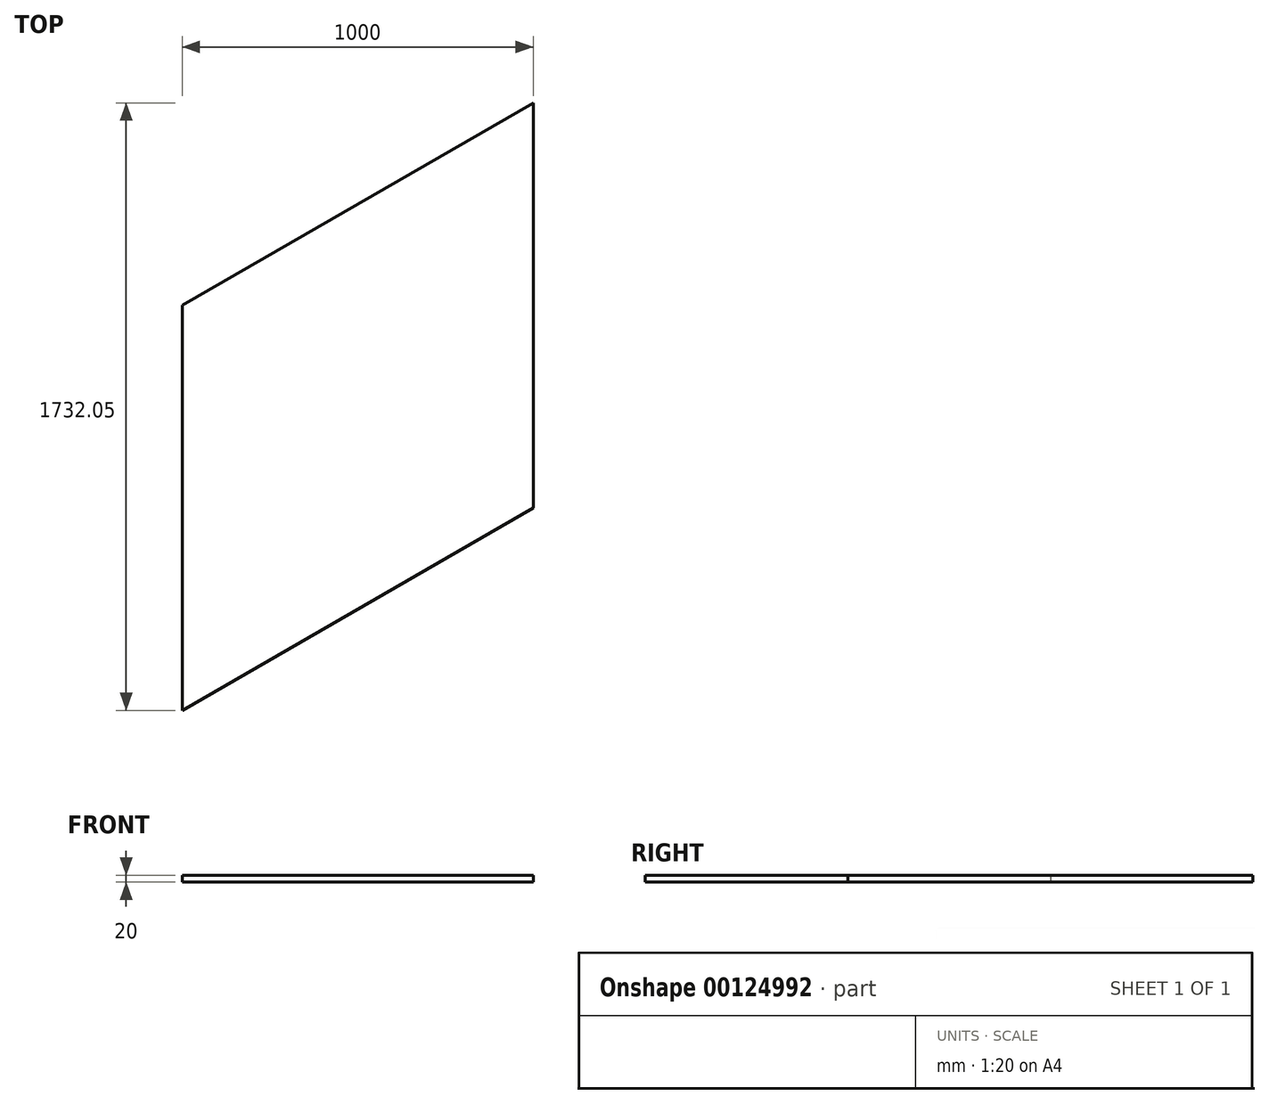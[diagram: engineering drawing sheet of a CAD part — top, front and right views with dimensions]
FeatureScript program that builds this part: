
annotation { "Feature Type Name" : "Feature", "Feature Type Description" : "" }
export const myFeature = defineFeature(function(context is Context, id is Id, definition is map)
    precondition{}
    {
        {
            var Q0;
            Q0=qCreatedBy(makeId("Top.planeOp"),FACE);
            var sketch = newSketch(context, id + "F0", { "sketchPlane" : qUnion([Q0])});
            skCircle(sketch, "E0.cCircle", {"center": v(0, 0) * mm, "radius": 1000 * mm, "construction": true});
            skLineSegment(sketch, "E0.0", {"start": v(1000, 577.35) * mm, "end": v(1000, -577.35) * mm});
            skLineSegment(sketch, "E0.1", {"start": v(1000, -577.35) * mm, "end": v(0, -1154.7) * mm});
            skLineSegment(sketch, "E0.2", {"start": v(0, -1154.7) * mm, "end": v(-1000, -577.35) * mm});
            skLineSegment(sketch, "E0.3", {"start": v(-1000, -577.35) * mm, "end": v(-1000, 577.35) * mm});
            skLineSegment(sketch, "E0.4", {"start": v(-1000, 577.35) * mm, "end": v(0, 1154.7) * mm});
            skLineSegment(sketch, "E0.5", {"start": v(0, 1154.7) * mm, "end": v(1000, 577.35) * mm});
            skPoint(sketch, "E0.0.midPoint", {"position": v(1000, 0) * mm});
            skLineSegment(sketch, "E1", {"start": v(-1000, -577.35) * mm, "end": v(0, 1154.7) * mm, "construction": true});
            skLineSegment(sketch, "E2.MirrorCS", {"start": v(0, 0) * mm, "end": v(0, 1154.7) * mm});
            skLineSegment(sketch, "E3.MirrorCS", {"start": v(-1000, -577.35) * mm, "end": v(0, 0) * mm});
            skLineSegment(sketch, "E4", {"start": v(0, 0) * mm, "end": v(1000, -577.35) * mm});
            skLineSegment(sketch, "E5", {"start": v(-500, 866.03) * mm, "end": v(-500, 288.68) * mm});
            skLineSegment(sketch, "E6", {"start": v(-500, 288.68) * mm, "end": v(0, 577.35) * mm});
            skLineSegment(sketch, "E7", {"start": v(-500, 288.68) * mm, "end": v(-1000, 0) * mm});
            skLineSegment(sketch, "E8", {"start": v(-500, 288.68) * mm, "end": v(-500, -288.68) * mm});
            skLineSegment(sketch, "E9.1.0", {"start": v(0, -577.35) * mm, "end": v(-500, -288.68) * mm});
            skLineSegment(sketch, "E9.1.1", {"start": v(-500, -866.03) * mm, "end": v(0, -577.35) * mm});
            skLineSegment(sketch, "E9.1.2", {"start": v(0, -577.35) * mm, "end": v(500, -866.03) * mm});
            skLineSegment(sketch, "E9.1.3", {"start": v(0, -577.35) * mm, "end": v(500, -288.68) * mm});
            skLineSegment(sketch, "E9.2.0", {"start": v(500, 288.68) * mm, "end": v(500, -288.68) * mm});
            skLineSegment(sketch, "E9.2.1", {"start": v(1000, 0) * mm, "end": v(500, 288.68) * mm});
            skLineSegment(sketch, "E9.2.2", {"start": v(500, 288.68) * mm, "end": v(500, 866.03) * mm});
            skLineSegment(sketch, "E9.2.3", {"start": v(500, 288.68) * mm, "end": v(0, 577.35) * mm});
            skSolve(sketch);
        }
        {
            var Q0;
            {var subQ4=sQuery(id+"F0.wireOp",EDGE,"E5");Q0=makeQuery(id+"F0.imprint","IMPRINT",FACE,{"disambiguationData":[TD([[makeQuery(id+"F0.imprint","IMPRINT",EDGE,{"derivedFrom":subQ4}),-1.0]])]});}
            var Q1;
            {var subQ3=sQuery(id+"F0.wireOp",EDGE,"E5");Q1=makeQuery(id+"F0.imprint","IMPRINT",FACE,{"disambiguationData":[TD([[makeQuery(id+"F0.imprint","IMPRINT",EDGE,{"derivedFrom":subQ3}),1.0]])]});}
            var Q2;
            {var subQ3=sQuery(id+"F0.wireOp",EDGE,"E6");Q2=makeQuery(id+"F0.imprint","IMPRINT",FACE,{"disambiguationData":[TD([[makeQuery(id+"F0.imprint","IMPRINT",EDGE,{"derivedFrom":subQ3}),-1.0]])]});}
            var Q3;
            {var subQ3=sQuery(id+"F0.wireOp",EDGE,"E7");Q3=makeQuery(id+"F0.imprint","IMPRINT",FACE,{"disambiguationData":[TD([[makeQuery(id+"F0.imprint","IMPRINT",EDGE,{"derivedFrom":subQ3}),1.0]])]});}
            extrude(context, id + "F1", {"entities" : qUnion([Q0, Q1, Q2, Q3]), "depth" : 20 * mm});
        }
    });
